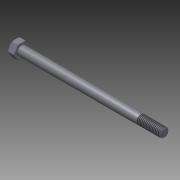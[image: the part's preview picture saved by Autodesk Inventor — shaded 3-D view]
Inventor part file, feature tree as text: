
AUTODESK INVENTOR PART (.ipt)
format: ipt  version: 2014 (Build 180170000, 170)  size: 169,472 bytes
history: native  units: mm (DEFAULTED — no unit token found)
features: sketch x3, extrude x1, chamfer x1, plane x1, fillet x1
ambient origin geometry x7: Origin, YZ Plane, XZ Plane, X Axis, Y Axis, Z Axis, Center Point
bodies: Solid1 (feature_tree), Body (feature_tree)
feature tree (7):
  extrude  "Head"  Depth=152.4mm
  chamfer  "Chamfer1"  Distance=6.8072mm
  plane  "Work Plane1"
  fillet  "Fillet2"  [1 undecoded]
  sketch  "Sketch1"  dims[d0=152.4mm d1=25.4mm]
  sketch  "Sketch2"  dims[d2=9.525mm]
  sketch  "Sketch4"  dims[d12=90.0deg d3=6.8072mm d4=0.0mm d5=30.0deg d21=90.0deg d6=0.973852mm d7=0.944662mm d8=0.0mm d9=0.0001mm d10=14.2748mm d11=14.2748mm d13=3.96885mm d14=9.8552mm d15=25.4mm d16=0.0mm d19=14.2748mm d55=45.0deg d58=0.0mm d62=-151.455437mm d63=0.762mm]
note: 1 required parameter value undecoded (feature->parameter linkage not recoverable at this tier; creation-order binding heuristic only, values carry confidence <= 0.55)
